# Revit family: Sink-Vessel-Lavatory-KOHLER-Veil_Essential-K-26408A
name_source: partatom
category: Plumbing Fixtures
units: mm (PartAtom-declared; Revit-internal decimal feet)

## family parameters
Cut with Voids When Loaded = No
Host = Face
OmniClass Number = 23.31.13.00
OmniClass Title = Sinks
Part Type = Normal
Room Calculation Point = No
Round Connector Dimension = Use Diameter
Shared = No

## types (1)
- 0-White
    ADA Compliant = No
    Assembly Code = D2010400
    CW Connection = No
    Cold Water Inlet = Cold Water Inlet
    Date Modified = 12/12/2022
    Default Elevation = 36"
    Description = Vessel, Round
    Drain Included = Yes
    Finish = Kohler-Vitreous_China-0-White
    HW Connection = No
    HWFU = 0
    Height = 7"
    Hot Water Inlet = Hot Water Inlet
    Length = 16 13/16"
    Manufacturer = Kohler Co.
    Master Format 2014 = 22 41 16
    Master Format 2014 Name = Residential Lavatories and Sinks
    Material = Viterious China
    Model = K-26408A-0
    Product Name = VEIL ESSENTIAL
    Type = 1
    URL = https://www.kohlerasiapacific.com
    Vent Connection = No
    WFU = 0
    Waste Connection = Yes
    Waste Water Outlet = Waste Water Outlet
    WaterSense Certified = No
    Width = 16 13/16"

## geometry (parser evidence)
native form markers: Sweep x5
no freeform markers — native parametric forms only
